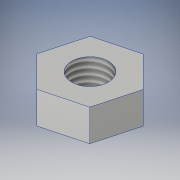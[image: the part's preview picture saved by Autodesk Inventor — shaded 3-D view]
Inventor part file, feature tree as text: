
AUTODESK INVENTOR PART (.ipt)
format: ipt  version: 2018 (Build 220112000, 112)  size: 103,936 bytes
history: native  units: in
note: dims shown in document units (in); Inventor stores cm internally (conversion verified against a paired STEP export)
features: extrude x1, thread x1, sketch x1
ambient origin geometry x8: Origin, YZ Plane, XZ Plane, XY Plane, X Axis, Y Axis, Z Axis, Center Point
bodies: Solid1 (feature_tree)
feature tree (3):
  extrude  "Extrusion1"  Depth=0.065in
  thread  "Thread1"  [1 undecoded]
  sketch  "Sketch1"  dims[d0=0.154in d1=0.075in d2=0.065in d3=0.0in d4=1.0in d5=0.0in]
note: 1 required parameter value undecoded (feature->parameter linkage not recoverable at this tier; creation-order binding heuristic only, values carry confidence <= 0.55)
